# Revit family: Ленточный арочный зенитный фонарь M8CITY_А_ВЕНТ_со_створками_2017
name_source: partatom
category: Оборудование
revit_build: Autodesk Revit 2017 (Build: 20170118_1100(x64)
units: mm (PartAtom-declared; Revit-internal decimal feet)

## family parameters
Всегда вертикально = Нет
Общий = Нет
Основа = Крыша
При загрузке вырезать с полостями = Нет
Размер круглого соединителя = Использовать диаметр
Тип детали = Нормальный
Точка расчета площади = Нет

## types (1)
- Зенитный фонарь M8CITY Л-А-створки вент
    ADSK_Завод-изготовитель = ООО ''Завод М8 Сити''
    ADSK_Код изделия = ТУ BY 191302027.002-2013
    ADSK_Количество = 1
    ADSK_Обозначение = M8CITY
    ADSK_Размер_Высота = 700 мм
    ADSK_Размер_Длина = 12000 мм
    ADSK_Размер_Ширина = 4000 мм
    N арок = 11
    N растров = 12
    Table 1 = Описание
    Table 2 = Маркировка
    URL = www.m8city.by
    Высота = 773 мм
    Высота основания = 700 мм
    Длина = 12000 мм
    Длина ПК = 5515 мм
    Длина проёма = 12000 мм
    Длина проёма ввод = 12000 мм
    Длина створки = 1900 мм
    Заполнение = 1
    Количество арок = 6
    Количество приводов = 3
    Количество створок = 3
    Количество створок ном = 3
    Количество типовых растров = 11
    Крайний растр = 745 мм
    Смещение массива = 2865 мм
    Смещение массива приводов = 2865 мм
    Типовой растр = 1060 мм
    Шаг массива = 3180 мм
    Шаг массива приводов = 3180 мм
    Шаг типовой = 1060 мм
    Ширина = 4000 мм
    Ширина проёма = 4000 мм
    Ширина проёма ввод = 4000 мм
